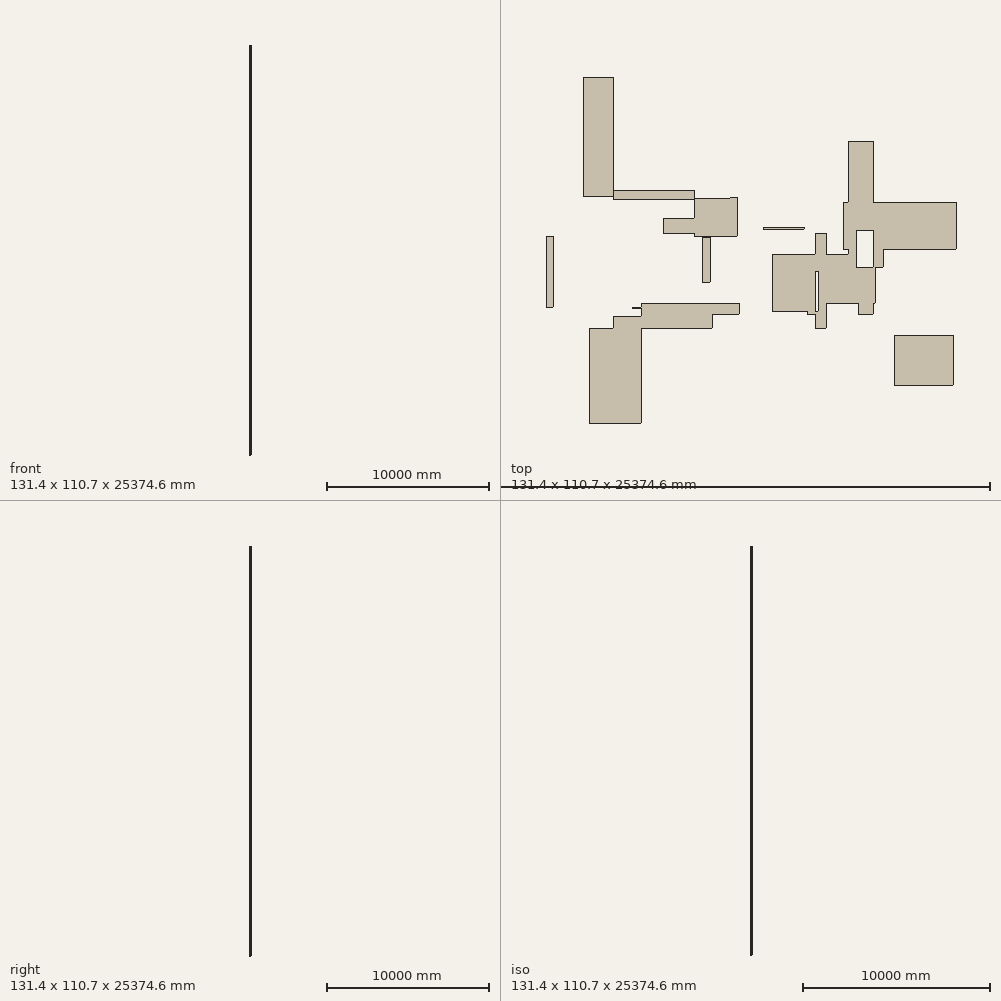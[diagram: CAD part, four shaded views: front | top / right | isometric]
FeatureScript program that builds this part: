
annotation { "Feature Type Name" : "Feature", "Feature Type Description" : "" }
export const myFeature = defineFeature(function(context is Context, id is Id, definition is map)
    precondition{}
    {
        {
            var Q0;
            Q0=qCreatedBy(makeId("Top.planeOp"),FACE);
            var sketch = newSketch(context, id + "F0", { "sketchPlane" : qUnion([Q0])});
            skLineSegment(sketch, "E0.bottom", {"start": v(-55.94, 45.24) * mm, "end": v(-29.83, 45.24) * mm});
            skLineSegment(sketch, "E0.top", {"start": v(-55.94, 5) * mm, "end": v(-29.83, 5) * mm});
            skLineSegment(sketch, "E0.left", {"start": v(-55.94, 45.24) * mm, "end": v(-55.94, 42.63) * mm});
            skLineSegment(sketch, "E0.right", {"start": v(-29.83, 45.24) * mm, "end": v(-29.83, 30.45) * mm});
            skLineSegment(sketch, "E1.bottom", {"start": v(30.86, 20.45) * mm, "end": v(22.16, 20.45) * mm});
            skLineSegment(sketch, "E1.top", {"start": v(30.86, 32.4) * mm, "end": v(22.16, 32.4) * mm});
            skLineSegment(sketch, "E1.left", {"start": v(30.86, 20.45) * mm, "end": v(30.86, 32.4) * mm});
            skLineSegment(sketch, "E1.right", {"start": v(22.16, 20.45) * mm, "end": v(22.16, 32.4) * mm});
            skLineSegment(sketch, "E2.bottom", {"start": v(-25.7, 57) * mm, "end": v(-55.72, 57) * mm});
            skLineSegment(sketch, "E2.top", {"start": v(-25.7, 42.42) * mm, "end": v(-55.72, 42.42) * mm});
            skLineSegment(sketch, "E2.left", {"start": v(-25.7, 42.63) * mm, "end": v(-25.7, 42.42) * mm});
            skLineSegment(sketch, "E2.right", {"start": v(-55.72, 57) * mm, "end": v(-55.72, 42.42) * mm});
            skLineSegment(sketch, "E3.bottom", {"start": v(-77.26, 30.45) * mm, "end": v(-74.86, 30.45) * mm});
            skLineSegment(sketch, "E3.top", {"start": v(-77.26, 7.61) * mm, "end": v(-74.86, 7.61) * mm});
            skLineSegment(sketch, "E3.left", {"start": v(-77.26, 30.45) * mm, "end": v(-77.26, 7.61) * mm});
            skLineSegment(sketch, "E3.right", {"start": v(-74.86, 30.45) * mm, "end": v(-74.86, 7.61) * mm});
            skLineSegment(sketch, "E4.bottom", {"start": v(-63.55, 1.08) * mm, "end": v(-23.96, 1.08) * mm});
            skLineSegment(sketch, "E4.top", {"start": v(-63.55, -29.37) * mm, "end": v(-46.8, -29.37) * mm});
            skLineSegment(sketch, "E4.left", {"start": v(-63.55, 1.08) * mm, "end": v(-63.55, -29.37) * mm});
            skLineSegment(sketch, "E4.right", {"start": v(5.4, 1.08) * mm, "end": v(5.4, -16.97) * mm});
            skLineSegment(sketch, "E5.bottom", {"start": v(11.71, -23.71) * mm, "end": v(20.2, -23.71) * mm});
            skLineSegment(sketch, "E5.right", {"start": v(20.2, -23.71) * mm, "end": v(20.2, -22.63) * mm});
            skLineSegment(sketch, "E6.bottom", {"start": v(19.55, 19.14) * mm, "end": v(-4.82, 19.14) * mm});
            skLineSegment(sketch, "E6.left", {"start": v(19.55, 19.14) * mm, "end": v(19.55, 61.12) * mm});
            skLineSegment(sketch, "E6.right", {"start": v(-28.96, 19.14) * mm, "end": v(-28.96, 42.63) * mm});
            skLineSegment(sketch, "E7.bottom", {"start": v(-65.3, 81.35) * mm, "end": v(-55.94, 81.35) * mm});
            skLineSegment(sketch, "E7.top", {"start": v(-65.3, 43.29) * mm, "end": v(-55.94, 43.29) * mm});
            skLineSegment(sketch, "E7.left", {"start": v(-65.3, 81.35) * mm, "end": v(-65.3, 43.29) * mm});
            skLineSegment(sketch, "E7.right", {"start": v(-55.94, 81.35) * mm, "end": v(-55.94, 43.29) * mm});
            skLineSegment(sketch, "E8.bottom", {"start": v(-27.22, 30.02) * mm, "end": v(-24.83, 30.02) * mm});
            skLineSegment(sketch, "E8.top", {"start": v(-27.22, 15.66) * mm, "end": v(-24.83, 15.66) * mm});
            skLineSegment(sketch, "E8.left", {"start": v(-27.22, 30.02) * mm, "end": v(-27.22, 15.66) * mm});
            skLineSegment(sketch, "E8.right", {"start": v(-24.83, 30.02) * mm, "end": v(-24.83, 15.66) * mm});
            skLineSegment(sketch, "E9.top", {"start": v(5.4, -15.01) * mm, "end": v(6.28, -15.01) * mm});
            skLineSegment(sketch, "E9.left", {"start": v(-23.96, 14.14) * mm, "end": v(-23.96, 1.08) * mm});
            skLineSegment(sketch, "E9.right", {"start": v(6.28, 14.14) * mm, "end": v(6.28, -15.01) * mm});
            skLineSegment(sketch, "E10.bottom", {"start": v(34.34, -17.4) * mm, "end": v(53.26, -17.4) * mm});
            skLineSegment(sketch, "E10.top", {"start": v(34.34, -1.3) * mm, "end": v(53.26, -1.3) * mm});
            skLineSegment(sketch, "E10.left", {"start": v(34.34, -17.4) * mm, "end": v(34.34, -1.3) * mm});
            skLineSegment(sketch, "E10.right", {"start": v(53.26, -17.4) * mm, "end": v(53.26, -1.3) * mm});
            skLineSegment(sketch, "E11.bottom", {"start": v(54.13, 26.32) * mm, "end": v(18.02, 26.32) * mm});
            skLineSegment(sketch, "E11.top", {"start": v(54.13, 41.33) * mm, "end": v(18.02, 41.33) * mm});
            skLineSegment(sketch, "E11.left", {"start": v(54.13, 26.32) * mm, "end": v(54.13, 41.33) * mm});
            skLineSegment(sketch, "E11.right", {"start": v(18.02, 26.32) * mm, "end": v(18.02, 41.33) * mm});
            skLineSegment(sketch, "E12.left", {"start": v(-5.25, 48.29) * mm, "end": v(-5.25, 29.36) * mm});
            skLineSegment(sketch, "E12.right", {"start": v(-16.13, 48.29) * mm, "end": v(-16.13, 29.36) * mm});
            skLineSegment(sketch, "E13.bottom", {"start": v(-4.82, 24.8) * mm, "end": v(22.16, 24.8) * mm});
            skLineSegment(sketch, "E13.top", {"start": v(-4.82, 6.3) * mm, "end": v(12.37, 6.3) * mm});
            skLineSegment(sketch, "E13.left", {"start": v(-4.82, 24.8) * mm, "end": v(-4.82, 6.3) * mm});
            skLineSegment(sketch, "E13.right", {"start": v(22.16, 24.8) * mm, "end": v(22.16, 6.3) * mm});
            skLineSegment(sketch, "E14.bottom", {"start": v(27.6, 5.44) * mm, "end": v(22.6, 5.44) * mm});
            skLineSegment(sketch, "E14.top", {"start": v(27.6, 60.9) * mm, "end": v(19.55, 60.9) * mm});
            skLineSegment(sketch, "E14.left", {"start": v(27.6, 5.44) * mm, "end": v(27.6, 60.9) * mm});
            skLineSegment(sketch, "E14.right", {"start": v(-42.67, 5.44) * mm, "end": v(-42.67, 12.61) * mm});
            skLineSegment(sketch, "E15.bottom", {"start": v(62.62, 9.13) * mm, "end": v(-4.82, 9.13) * mm});
            skLineSegment(sketch, "E15.right", {"start": v(-46.8, 9.13) * mm, "end": v(-46.8, -43.5) * mm});
            skLineSegment(sketch, "E16.bottom", {"start": v(-55.94, -28.93) * mm, "end": v(-46.8, -28.93) * mm});
            skLineSegment(sketch, "E16.top", {"start": v(-29.83, 30.45) * mm, "end": v(-15.48, 30.45) * mm});
            skLineSegment(sketch, "E16.left", {"start": v(-55.94, -28.93) * mm, "end": v(-55.94, 30.45) * mm});
            skLineSegment(sketch, "E17.bottom", {"start": v(-7.65, 33.5) * mm, "end": v(5.4, 33.5) * mm});
            skLineSegment(sketch, "E17.top", {"start": v(-7.65, 32.63) * mm, "end": v(5.4, 32.63) * mm});
            skLineSegment(sketch, "E17.left", {"start": v(-7.65, 33.5) * mm, "end": v(-7.65, 32.63) * mm});
            skLineSegment(sketch, "E17.right", {"start": v(5.4, 33.5) * mm, "end": v(5.4, 32.63) * mm});
            skLineSegment(sketch, "E18.bottom", {"start": v(12.37, 31.32) * mm, "end": v(8.89, 31.32) * mm});
            skLineSegment(sketch, "E18.top", {"start": v(12.37, 0.87) * mm, "end": v(8.89, 0.87) * mm});
            skLineSegment(sketch, "E18.left", {"start": v(12.37, 31.32) * mm, "end": v(12.37, 0.87) * mm});
            skLineSegment(sketch, "E18.right", {"start": v(8.89, 31.32) * mm, "end": v(8.89, 0.87) * mm});
            skLineSegment(sketch, "E19.bottom", {"start": v(-46.37, 7.4) * mm, "end": v(-49.63, 7.4) * mm});
            skLineSegment(sketch, "E19.top", {"start": v(-46.37, 7.83) * mm, "end": v(-49.63, 7.83) * mm});
            skLineSegment(sketch, "E19.left", {"start": v(-46.37, 7.4) * mm, "end": v(-46.37, 7.83) * mm});
            skLineSegment(sketch, "E19.right", {"start": v(-49.63, 7.4) * mm, "end": v(-49.63, 7.83) * mm});
            skLineSegment(sketch, "E20.bottom", {"start": v(-39.84, 36.33) * mm, "end": v(-16.13, 36.33) * mm});
            skLineSegment(sketch, "E20.top", {"start": v(-39.84, 31.54) * mm, "end": v(-16.13, 31.54) * mm});
            skLineSegment(sketch, "E20.left", {"start": v(-39.84, 36.33) * mm, "end": v(-39.84, 31.54) * mm});
            skLineSegment(sketch, "E20.right", {"start": v(-7.65, 36.33) * mm, "end": v(-7.65, 31.54) * mm});
            skLineSegment(sketch, "E21.bottom", {"start": v(22.6, 21.97) * mm, "end": v(28.25, 21.97) * mm});
            skLineSegment(sketch, "E21.left", {"start": v(22.6, 21.97) * mm, "end": v(22.6, 5.44) * mm});
            skLineSegment(sketch, "E21.right", {"start": v(28.25, 21.97) * mm, "end": v(28.25, 9.13) * mm});
            skLineSegment(sketch, "E22.bottom", {"start": v(28.25, -16.97) * mm, "end": v(20.2, -16.97) * mm});
            skLineSegment(sketch, "E22.top", {"start": v(28.25, -22.63) * mm, "end": v(2.36, -22.63) * mm});
            skLineSegment(sketch, "E22.left", {"start": v(28.25, -16.97) * mm, "end": v(28.25, -22.63) * mm});
            skLineSegment(sketch, "E23.top", {"start": v(-28.53, 1.3) * mm, "end": v(-30.49, 1.3) * mm});
            skLineSegment(sketch, "E23.left", {"start": v(-28.53, 1.08) * mm, "end": v(-28.53, 1.3) * mm});
            skLineSegment(sketch, "E23.right", {"start": v(-30.49, 1.08) * mm, "end": v(-30.49, 1.3) * mm});
            skLineSegment(sketch, "E24.bottom", {"start": v(-18.3, 37.41) * mm, "end": v(-16.13, 37.41) * mm});
            skLineSegment(sketch, "E24.top", {"start": v(-18.3, 43.07) * mm, "end": v(-16.13, 43.07) * mm});
            skLineSegment(sketch, "E24.left", {"start": v(-18.3, 37.41) * mm, "end": v(-18.3, 43.07) * mm});
            skLineSegment(sketch, "E24.right", {"start": v(-6.78, 37.41) * mm, "end": v(-6.78, 43.07) * mm});
            skLineSegment(sketch, "E25.bottom", {"start": v(9.76, 42.63) * mm, "end": v(-6.78, 42.63) * mm});
            skLineSegment(sketch, "E25.left", {"start": v(9.76, 42.63) * mm, "end": v(9.76, 6.3) * mm});
            skLineSegment(sketch, "E25.right", {"start": v(-60.5, 42.63) * mm, "end": v(-60.5, -15.88) * mm});
            skPoint(sketch, "E26.orphan", {"position": v(-42.67, 60.9) * mm});
            skLineSegment(sketch, "E27.trimOffspring", {"start": v(-42.67, 42.42) * mm, "end": v(-42.67, 42.63) * mm});
            skPoint(sketch, "E28.right.end.orphan", {"position": v(-42.67, 33.17) * mm});
            skLineSegment(sketch, "E29.trimOffspring", {"start": v(-55.94, 30.45) * mm, "end": v(-55.94, 5) * mm});
            skLineSegment(sketch, "E30.trimOffspring", {"start": v(-55.94, 42.63) * mm, "end": v(-60.5, 42.63) * mm});
            skLineSegment(sketch, "E31.trimOffspring", {"start": v(-15.48, 1.08) * mm, "end": v(-15.48, 9.13) * mm});
            skLineSegment(sketch, "E32.trimOffspring", {"start": v(-29.83, 9.13) * mm, "end": v(-29.83, 5) * mm});
            skLineSegment(sketch, "E33.trimOffspring", {"start": v(-46.8, -15.88) * mm, "end": v(-60.5, -15.88) * mm});
            skLineSegment(sketch, "E34.trimOffspring", {"start": v(-15.48, 5.44) * mm, "end": v(-42.67, 5.44) * mm});
            skLineSegment(sketch, "E35.trimOffspring", {"start": v(-15.48, 9.13) * mm, "end": v(-46.8, 9.13) * mm});
            skLineSegment(sketch, "E36.trimOffspring", {"start": v(-24.83, 19.14) * mm, "end": v(-28.96, 19.14) * mm});
            skLineSegment(sketch, "E37.trimOffspring", {"start": v(-28.96, 57) * mm, "end": v(-28.96, 61.12) * mm});
            skLineSegment(sketch, "E38.trimOffspring", {"start": v(-16.13, 42.63) * mm, "end": v(-29.83, 42.63) * mm});
            skLineSegment(sketch, "E39.trimOffspring", {"start": v(5.4, -22.63) * mm, "end": v(5.4, -29.37) * mm});
            skLineSegment(sketch, "E40.trimOffspring", {"start": v(5.4, -16.97) * mm, "end": v(2.36, -16.97) * mm});
            skLineSegment(sketch, "E41.trimOffspring", {"start": v(12.37, 5.44) * mm, "end": v(6.28, 5.44) * mm});
            skLineSegment(sketch, "E42.trimOffspring", {"start": v(9.76, 5.44) * mm, "end": v(9.76, -15.88) * mm});
            skSolve(sketch);
        }
        {
            var Q0;
            Q0 = qSketchRegion(id + "F0", true);
            extrude(context, id + "F1", {"entities" : qUnion([Q0]), "depth" : 25374.6 * mm, "offsetDistance" : 25.4 * mm});
        }
    });
